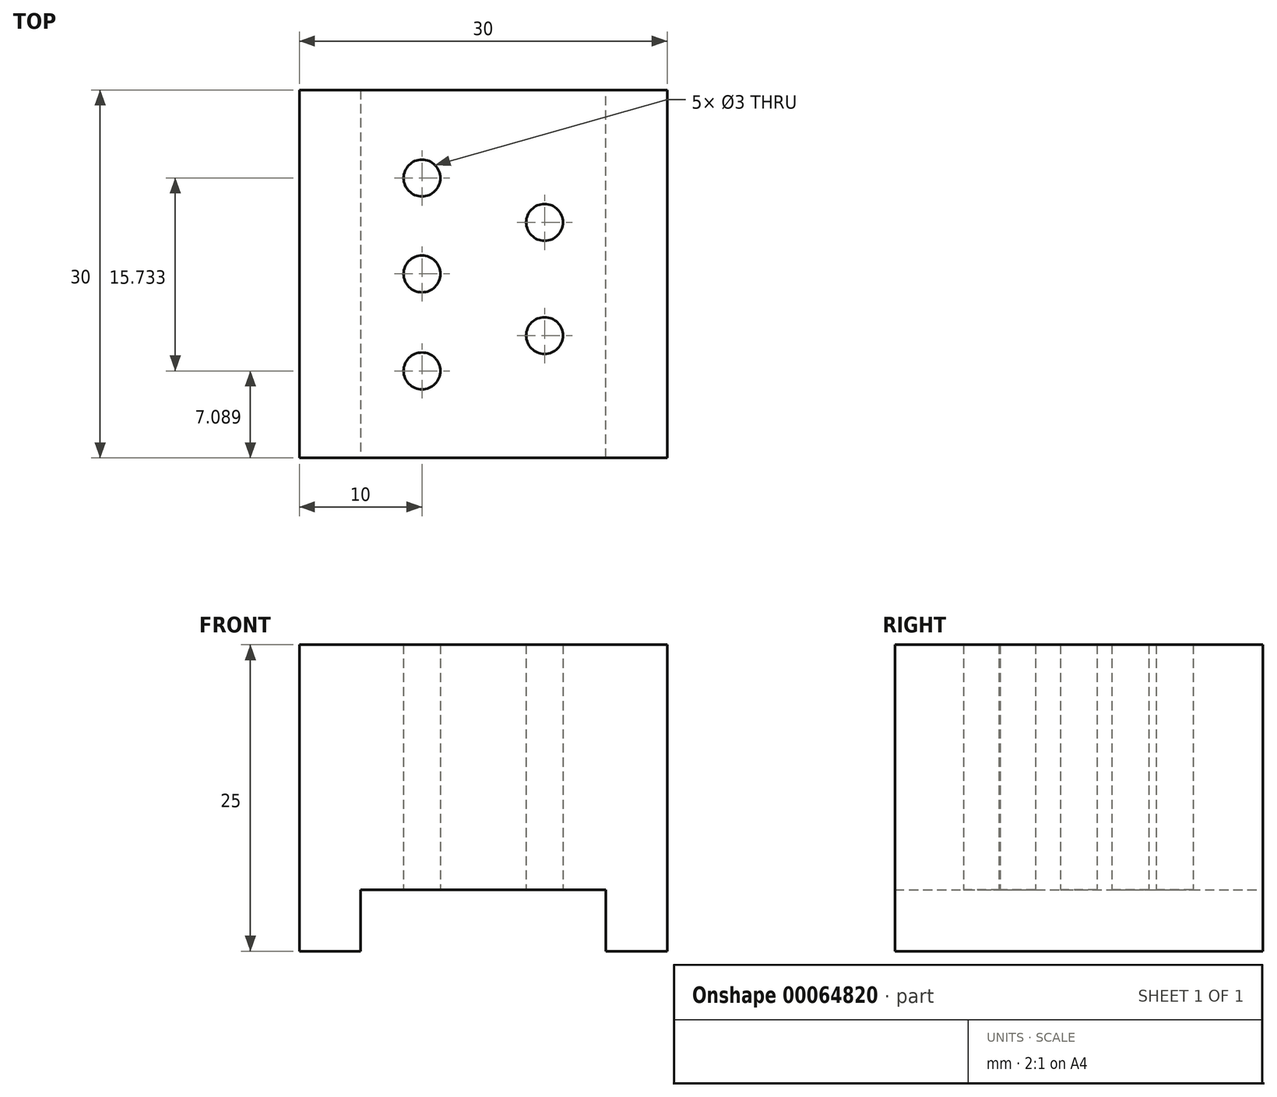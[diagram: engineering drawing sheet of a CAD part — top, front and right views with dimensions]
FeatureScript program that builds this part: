
annotation { "Feature Type Name" : "Feature", "Feature Type Description" : "" }
export const myFeature = defineFeature(function(context is Context, id is Id, definition is map)
    precondition{}
    {
        {
            var Q0;
            Q0=qCreatedBy(makeId("Top.planeOp"),FACE);
            var sketch = newSketch(context, id + "F0", { "sketchPlane" : qUnion([Q0])});
            skLineSegment(sketch, "E0.rect.bottom", {"start": v(-15, 15) * mm, "end": v(15, 15) * mm});
            skLineSegment(sketch, "E0.rect.top", {"start": v(-15, -15) * mm, "end": v(15, -15) * mm});
            skLineSegment(sketch, "E0.rect.left", {"start": v(-15, 15) * mm, "end": v(-15, -15) * mm});
            skLineSegment(sketch, "E0.rect.right", {"start": v(15, 15) * mm, "end": v(15, -15) * mm});
            skPoint(sketch, "E0.rect.middle", {"position": v(0, 0) * mm});
            skCircle(sketch, "E1", {"center": v(-5, 7.82) * mm, "radius": 1.5 * mm});
            skCircle(sketch, "E2", {"center": v(-5, 0) * mm, "radius": 1.5 * mm});
            skCircle(sketch, "E3", {"center": v(-5, -7.91) * mm, "radius": 1.5 * mm});
            skCircle(sketch, "E4", {"center": v(5, -5.03) * mm, "radius": 1.5 * mm});
            skCircle(sketch, "E5", {"center": v(5, 4.2) * mm, "radius": 1.5 * mm});
            skLineSegment(sketch, "E6.bottom", {"start": v(-15, -15) * mm, "end": v(-10, -15) * mm});
            skLineSegment(sketch, "E6.top", {"start": v(-15, 15) * mm, "end": v(-10, 15) * mm});
            skLineSegment(sketch, "E6.left", {"start": v(-15, -15) * mm, "end": v(-15, 15) * mm});
            skLineSegment(sketch, "E7.bottom", {"start": v(15, 15) * mm, "end": v(10, 15) * mm});
            skLineSegment(sketch, "E7.top", {"start": v(15, -15) * mm, "end": v(10, -15) * mm});
            skCircle(sketch, "E8", {"center": v(-5, 7.82) * mm, "radius": 3.5 * mm});
            skCircle(sketch, "E9", {"center": v(-5, 0) * mm, "radius": 3.5 * mm});
            skCircle(sketch, "E10", {"center": v(-5, -7.91) * mm, "radius": 3.5 * mm});
            skCircle(sketch, "E11", {"center": v(5, -5.03) * mm, "radius": 3.5 * mm});
            skCircle(sketch, "E12", {"center": v(5, 4.2) * mm, "radius": 3.5 * mm});
            skSolve(sketch);
        }
        {
            var Q0;
            Q0=makeQuery(id+"F0.imprint","IMPRINT",FACE,{"disambiguationData":[TD([[makeQuery(id+"F0.imprint","IMPRINT",EDGE,{"derivedFrom":sQuery(id+"F0.wireOp",EDGE,"E5")}),-1.0]])]});
            var Q1;
            Q1=makeQuery(id+"F0.imprint","IMPRINT",FACE,{"disambiguationData":[TD([[makeQuery(id+"F0.imprint","IMPRINT",EDGE,{"derivedFrom":sQuery(id+"F0.wireOp",EDGE,"E1")}),-1.0]])]});
            var Q2;
            Q2=makeQuery(id+"F0.imprint","IMPRINT",FACE,{"disambiguationData":[TD([[makeQuery(id+"F0.imprint","IMPRINT",EDGE,{"derivedFrom":sQuery(id+"F0.wireOp",EDGE,"E2")}),-1.0]])]});
            var Q3;
            Q3=makeQuery(id+"F0.imprint","IMPRINT",FACE,{"disambiguationData":[TD([[makeQuery(id+"F0.imprint","IMPRINT",EDGE,{"derivedFrom":sQuery(id+"F0.wireOp",EDGE,"E0.rect.bottom")}),-1.0]])]});
            var Q4;
            Q4=makeQuery(id+"F0.imprint","IMPRINT",FACE,{"disambiguationData":[TD([[makeQuery(id+"F0.imprint","IMPRINT",EDGE,{"derivedFrom":sQuery(id+"F0.wireOp",EDGE,"E3")}),-1.0]])]});
            var Q5;
            Q5=makeQuery(id+"F0.imprint","IMPRINT",FACE,{"disambiguationData":[TD([[makeQuery(id+"F0.imprint","IMPRINT",EDGE,{"derivedFrom":sQuery(id+"F0.wireOp",EDGE,"E4")}),-1.0]])]});
            extrude(context, id + "F1", {"entities" : qUnion([Q0, Q1, Q2, Q3, Q4, Q5]), "depth" : 20 * mm});
        }
        {
            var Q0;
            Q0=makeQuery(id+"F1.opExtrude","CAP_FACE",FACE,{"disambiguationData":[OSD([sQuery(id+"F0.wireOp",EDGE,"E0.rect.bottom"),sQuery(id+"F0.wireOp",EDGE,"E0.rect.top"),sQuery(id+"F0.wireOp",EDGE,"E1"),sQuery(id+"F0.wireOp",EDGE,"E2"),sQuery(id+"F0.wireOp",EDGE,"E3"),sQuery(id+"F0.wireOp",EDGE,"E4"),sQuery(id+"F0.wireOp",EDGE,"E5"),sQuery(id+"F0.wireOp",EDGE,"E6.bottom"),sQuery(id+"F0.wireOp",EDGE,"E6.top"),sQuery(id+"F0.wireOp",EDGE,"E6.left"),sQuery(id+"F0.wireOp",EDGE,"E7.bottom"),sQuery(id+"F0.wireOp",EDGE,"E7.top"),sQuery(id+"F0.wireOp",EDGE,"E0.rect.right")])],"isStart":true});
            var sketch = newSketch(context, id + "F2", { "sketchPlane" : qUnion([Q0])});
            skLineSegment(sketch, "E13.bottom", {"start": v(-15, -15) * mm, "end": v(-10, -15) * mm});
            skLineSegment(sketch, "E13.top", {"start": v(-15, 15) * mm, "end": v(-10, 15) * mm});
            skLineSegment(sketch, "E13.left", {"start": v(-15, -15) * mm, "end": v(-15, 15) * mm});
            skLineSegment(sketch, "E13.right", {"start": v(-10, -15) * mm, "end": v(-10, 15) * mm});
            skLineSegment(sketch, "E14.bottom", {"start": v(15, 15) * mm, "end": v(10, 15) * mm});
            skLineSegment(sketch, "E14.top", {"start": v(15, -15) * mm, "end": v(10, -15) * mm});
            skLineSegment(sketch, "E14.left", {"start": v(15, 15) * mm, "end": v(15, -15) * mm});
            skLineSegment(sketch, "E14.right", {"start": v(10, 15) * mm, "end": v(10, -15) * mm});
            skSolve(sketch);
        }
        {
            var Q0;
            Q0=makeQuery(id+"F2.imprint","IMPRINT",FACE,{"disambiguationData":[TD([[makeQuery(id+"F2.imprint","IMPRINT",EDGE,{"derivedFrom":sQuery(id+"F2.wireOp",EDGE,"E14.bottom")}),-1.0]])]});
            var Q1;
            Q1=makeQuery(id+"F2.imprint","IMPRINT",FACE,{"disambiguationData":[TD([[makeQuery(id+"F2.imprint","IMPRINT",EDGE,{"derivedFrom":sQuery(id+"F2.wireOp",EDGE,"E13.bottom")}),1.0]])]});
            extrude(context, id + "F3", {"entities" : qUnion([Q0, Q1]), "operationType" : NewBodyOperationType.ADD, "depth" : 5 * mm});
        }
    });
